# Revit family: Indoor_Wall Lamp_Santa&Cole_Comodín
name_source: partatom
category: Luminarias
revit_build: Autodesk Revit 2018 (Build: 20190510_1515(x64)
units: mm (PartAtom-declared; Revit-internal decimal feet)

## family parameters
Compartido = No
Corte con vacíos al cargar = No
Cota de conector redondo = Diámetro de uso
Número OmniClass = 23.80.70.00
Origen de luz = Sí
Punto de cálculo de habitación = No
Se basa en plano de trabajo = Sí
Siempre vertical = Sí
Tipo de pieza = Normal
Título OmniClass = Lighting

## types (14) — shared parameters
Assembly instructions - CE = https://www.santacole.com
Assembly instructions - UL = https://www.santacole.com
Cambio de temperatura de color de luz atenuada = <Ninguno>
Carga aparente = 5 VA
Code = COM01+COMxx
Elevación por defecto = 1219 mm
Energy Label = https://www.santacole.com
Fabricante = Santa & Cole
Filtro de color = 16777215
Manufacturer website = https://www.santacole.com
Modelo = Comodín
Structure Material = Santa & Cole - Chrome Metal
Tamaño de símbolo de origen de luz = 50 mm  [stored 0.164042 ft]
Technical Information = https://www.santacole.com
URL = https://www.santacole.com
Voltaje (90-305 V) = 220 V

## per-type parameters (varying)
| type | Lampshade Material | Visibility_Beige Parchment_Cuadrado | Visibility_Beige Parchment_Rectangular | Visibility_Cuadrado | Visibility_Rectangular |
| Comodín Cuadrado - Stitched Beige Parchment | Santa & Cole - Beige Cardboard | Sí | No | Sí | No |
| Comodín Cuadrado - Natural Ribbon | Santa & Cole - Natural Ribbon | No | No | Sí | No |
| Comodín Cuadrado - Red-amber Ribbon | Santa & Cole - Red-amber Ribbon | No | No | Sí | No |
| Comodín Cuadrado - Black Ribbon | Santa & Cole - Black Ribbon | No | No | Sí | No |
| Comodín Cuadrado - Terracota Raw Color Ribbon | Santa & Cole - Terracota Raw Color Ribbon | No | No | Sí | No |
| Comodín Cuadrado - Mustard Raw Color Ribbon | Santa & Cole - Mustard Raw Color Ribbon | No | No | Sí | No |
| Comodín Cuadrado - Green Raw Color Ribbon | Santa & Cole - Green Raw Color Ribbon | No | No | Sí | No |
| Comodín Rectangular - Stitched Beige Parchment | Santa & Cole - Beige Cardboard | No | Sí | No | Sí |
| Comodín Rectangular - Natural Ribbon | Santa & Cole - Natural Ribbon | No | No | No | Sí |
| Comodín Rectangular - Red-amber Ribbon | Santa & Cole - Red-amber Ribbon | No | No | No | Sí |
| Comodín Rectangular - Black Ribbon | Santa & Cole - Black Ribbon | No | No | No | Sí |
| Comodín Rectangular - Terracota Raw Color Ribbon | Santa & Cole - Terracota Raw Color Ribbon | No | No | No | Sí |
| Comodín Rectangular - Mustard Raw Color Ribbon | Santa & Cole - Mustard Raw Color Ribbon | No | No | No | Sí |
| Comodín Rectangular - Green Raw Color Ribbon | Santa & Cole - Green Raw Color Ribbon | No | No | No | Sí |

note: [stored X ft] marks values corroborated as IEEE doubles in the binary element streams (Revit-internal decimal feet)
